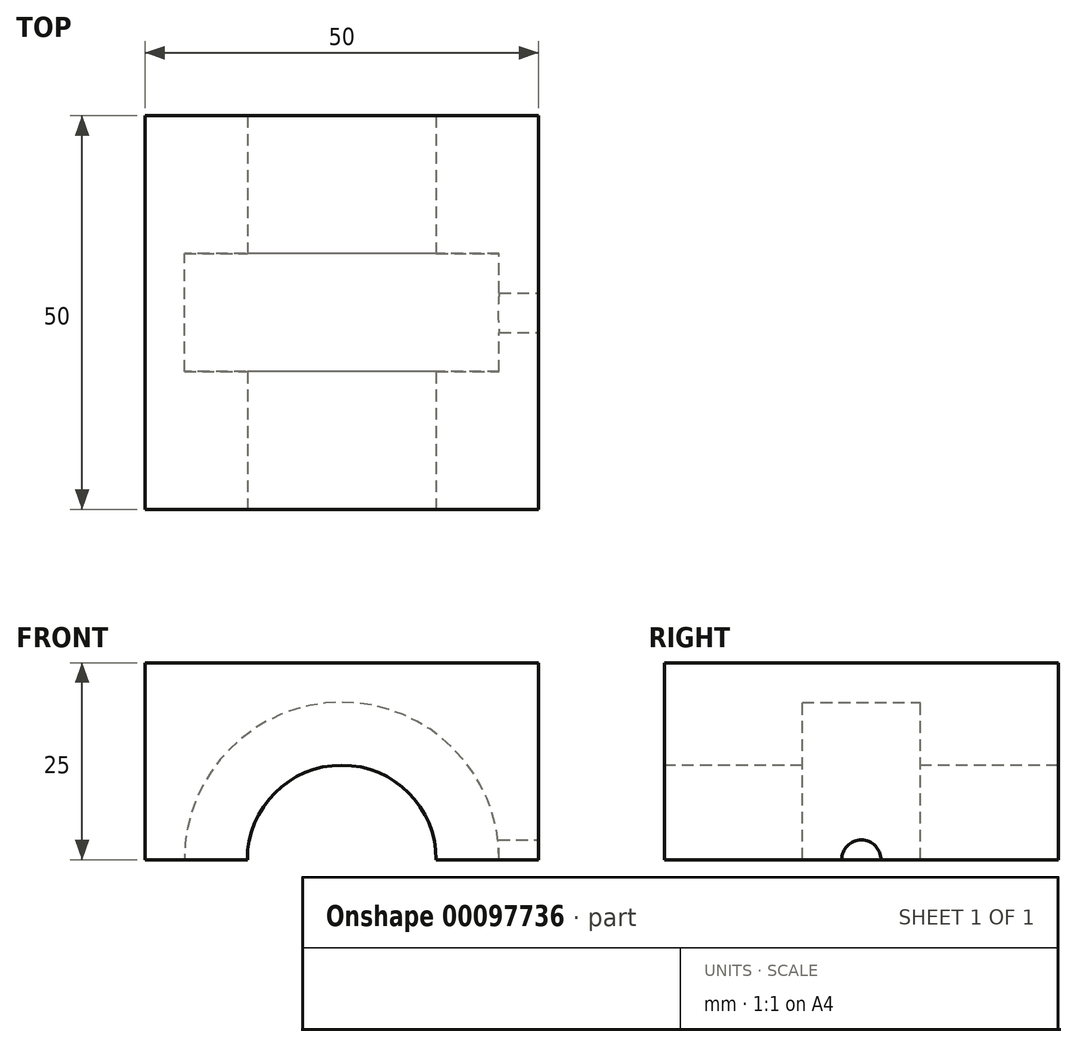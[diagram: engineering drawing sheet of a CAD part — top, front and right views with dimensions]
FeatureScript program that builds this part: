
annotation { "Feature Type Name" : "Feature", "Feature Type Description" : "" }
export const myFeature = defineFeature(function(context is Context, id is Id, definition is map)
    precondition{}
    {
        {
            var Q0;
            Q0=qCreatedBy(makeId("Front.planeOp"),FACE);
            var sketch = newSketch(context, id + "F0", { "sketchPlane" : qUnion([Q0])});
            skLineSegment(sketch, "E0.bottom", {"start": v(-25, 0) * mm, "end": v(25, 0) * mm});
            skLineSegment(sketch, "E0.top", {"start": v(-25, 25) * mm, "end": v(25, 25) * mm});
            skLineSegment(sketch, "E0.left", {"start": v(-25, 0) * mm, "end": v(-25, 25) * mm});
            skLineSegment(sketch, "E0.right", {"start": v(25, 0) * mm, "end": v(25, 25) * mm});
            skSolve(sketch);
        }
        {
            var Q0;
            Q0=makeQuery(id+"F0.imprint","IMPRINT",FACE,{"disambiguationData":[TD([[makeQuery(id+"F0.imprint","IMPRINT",EDGE,{"derivedFrom":sQuery(id+"F0.wireOp",EDGE,"E0.bottom")}),1.0]])]});
            extrude(context, id + "F1", {"entities" : qUnion([Q0]), "endBound" : BoundingType.SYMMETRIC, "depth" : 50 * mm});
        }
        {
            var Q0;
            Q0=makeQuery(id+"F1.opExtrude","SWEPT_FACE",FACE,{"disambiguationData":[OSD([sQuery(id+"F0.wireOp",EDGE,"E0.right")])]});
            var sketch = newSketch(context, id + "F2", { "sketchPlane" : qUnion([Q0])});
            skCircle(sketch, "E1", {"center": v(0, 0) * mm, "radius": 2.5 * mm});
            skSolve(sketch);
        }
        {
            var Q0;
            {var subQ0=sQuery(id+"F2.wireOp",EDGE,"E1");var subQ1=makeQuery(id+"F1.opExtrude","SWEPT_EDGE",EDGE,{"disambiguationData":[OSD([sQuery(id+"F0.wireOp",EDGE,"E0.bottom"),sQuery(id+"F0.wireOp",EDGE,"E0.right")])]});var subQ2=makeQuery(id+"F2.imprint","INTERSECT",VERTEX,{"disambiguationData":[OD(0.0)],"derivedFrom":[subQ1,subQ0]});Q0=makeQuery(id+"F2.imprint","IMPRINT",FACE,{"disambiguationData":[TD([[makeQuery(id+"F2.imprint","IMPRINT",EDGE,{"disambiguationData":[TD([[subQ2,-1.0]])],"derivedFrom":subQ0}),1.0]])]});}
            extrude(context, id + "F3", {"entities" : qUnion([Q0]), "operationType" : NewBodyOperationType.REMOVE, "oppositeDirection" : true, "depth" : 25 * mm});
        }
        {
            var Q0;
            Q0=qCreatedBy(makeId("Front.planeOp"),FACE);
            var sketch = newSketch(context, id + "F4", { "sketchPlane" : qUnion([Q0])});
            skCircle(sketch, "E2", {"center": v(0, 0) * mm, "radius": 20 * mm});
            skSolve(sketch);
        }
        {
            var Q0;
            Q0 = qSketchRegion(id + "F4", true);
            extrude(context, id + "F5", {"entities" : qUnion([Q0]), "operationType" : NewBodyOperationType.REMOVE, "endBound" : BoundingType.SYMMETRIC, "depth" : 15 * mm});
        }
        {
            var Q0;
            Q0=makeQuery(id+"F1.opExtrude","CAP_FACE",FACE,{"disambiguationData":[OSD([sQuery(id+"F0.wireOp",EDGE,"E0.bottom"),sQuery(id+"F0.wireOp",EDGE,"E0.top"),sQuery(id+"F0.wireOp",EDGE,"E0.left"),sQuery(id+"F0.wireOp",EDGE,"E0.right")])],"isStart":false});
            var sketch = newSketch(context, id + "F6", { "sketchPlane" : qUnion([Q0])});
            skCircle(sketch, "E3", {"center": v(0, 0) * mm, "radius": 12 * mm});
            skSolve(sketch);
        }
        {
            var Q0;
            {var subQ0=sQuery(id+"F6.wireOp",EDGE,"E3");var subQ1=makeQuery(id+"F1.opExtrude","CAP_EDGE",EDGE,{"disambiguationData":[OSD([sQuery(id+"F0.wireOp",EDGE,"E0.bottom")])],"isStart":false});var subQ2=makeQuery(id+"F6.imprint","INTERSECT",VERTEX,{"disambiguationData":[OD(0.0)],"derivedFrom":[subQ1,subQ0]});Q0=makeQuery(id+"F6.imprint","IMPRINT",FACE,{"disambiguationData":[TD([[makeQuery(id+"F6.imprint","IMPRINT",EDGE,{"disambiguationData":[TD([[subQ2,1.0]])],"derivedFrom":subQ0}),1.0]])]});}
            extrude(context, id + "F7", {"entities" : qUnion([Q0]), "operationType" : NewBodyOperationType.REMOVE, "endBound" : BoundingType.THROUGH_ALL, "oppositeDirection" : true, "depth" : 25 * mm});
        }
    });
